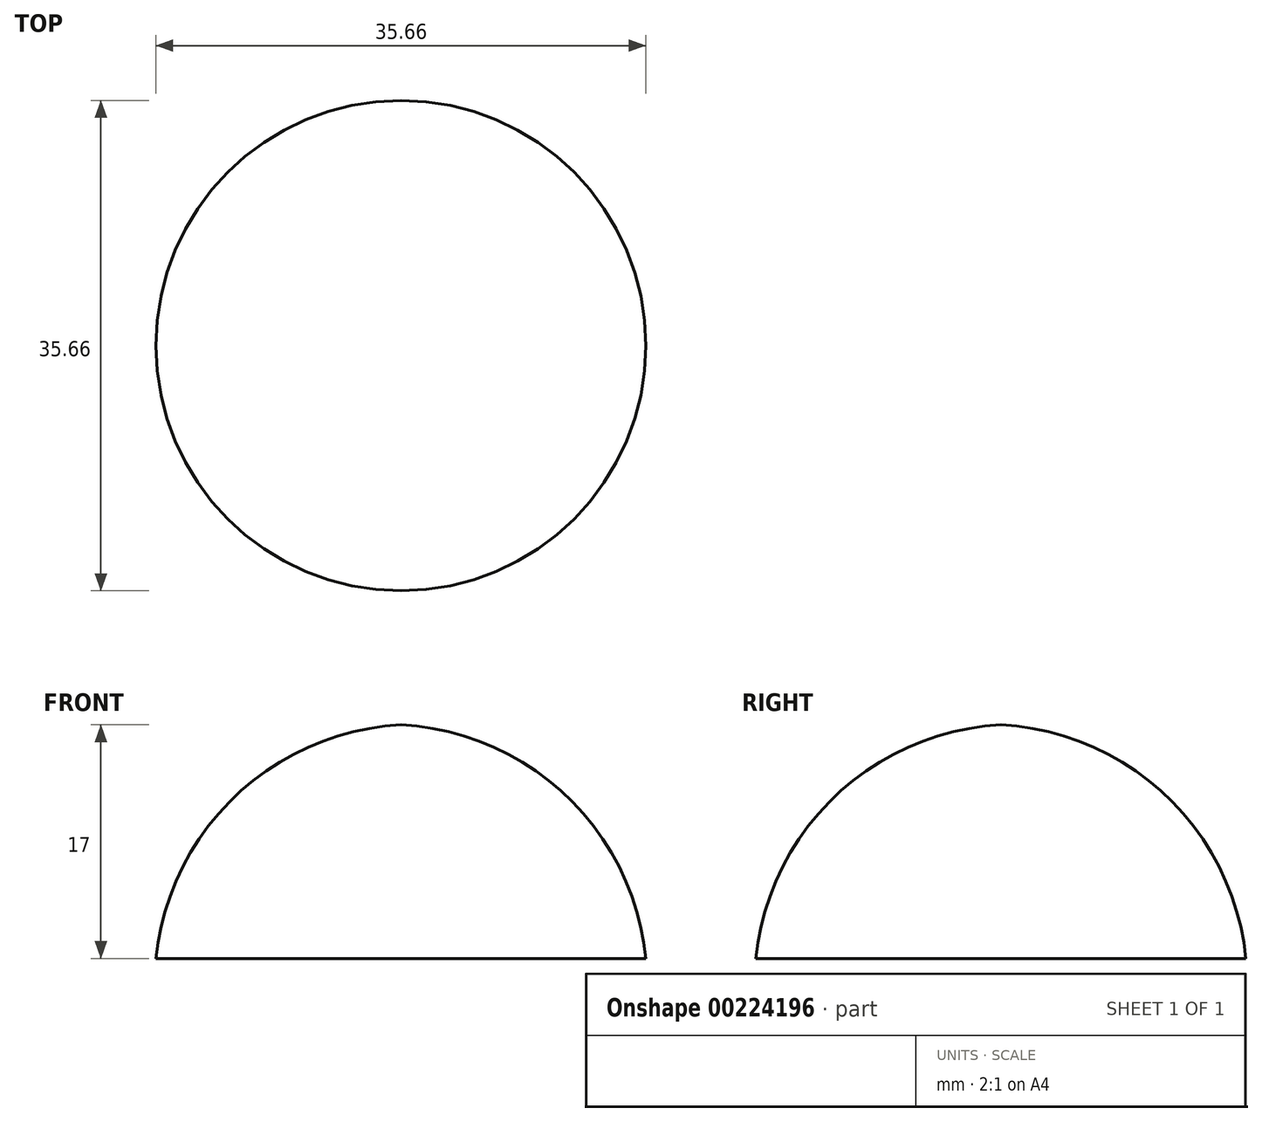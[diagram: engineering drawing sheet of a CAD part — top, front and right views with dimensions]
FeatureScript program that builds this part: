
annotation { "Feature Type Name" : "Feature", "Feature Type Description" : "" }
export const myFeature = defineFeature(function(context is Context, id is Id, definition is map)
    precondition{}
    {
        {
            var Q0;
            Q0=qCreatedBy(makeId("Front.planeOp"),FACE);
            var sketch = newSketch(context, id + "F0", { "sketchPlane" : qUnion([Q0])});
            skLineSegment(sketch, "E0", {"start": v(0, 28.3) * mm, "end": v(0, 11.3) * mm});
            skLineSegment(sketch, "E1", {"start": v(17.83, 11.3) * mm, "end": v(0, 11.3) * mm});
            skArc(sketch, "E2", {"start": v(17.83, 11.3) * mm, "mid": v(12.06, 23.1) * mm, "end": v(0, 28.3) * mm});
            skSolve(sketch);
        }
        {
            var Q0;
            Q0=makeQuery(id+"F0.imprint","IMPRINT",FACE,{"disambiguationData":[TD([[makeQuery(id+"F0.imprint","IMPRINT",EDGE,{"derivedFrom":sQuery(id+"F0.wireOp",EDGE,"E0")}),1.0]])]});
            var Q1;
            Q1=sQuery(id+"F0.wireOp",EDGE,"E0");
            revolve(context, id + "F1", {"entities" : qUnion([Q0]), "axis" : qUnion([Q1]), "revolveType" : RevolveType.FULL});
        }
    });
